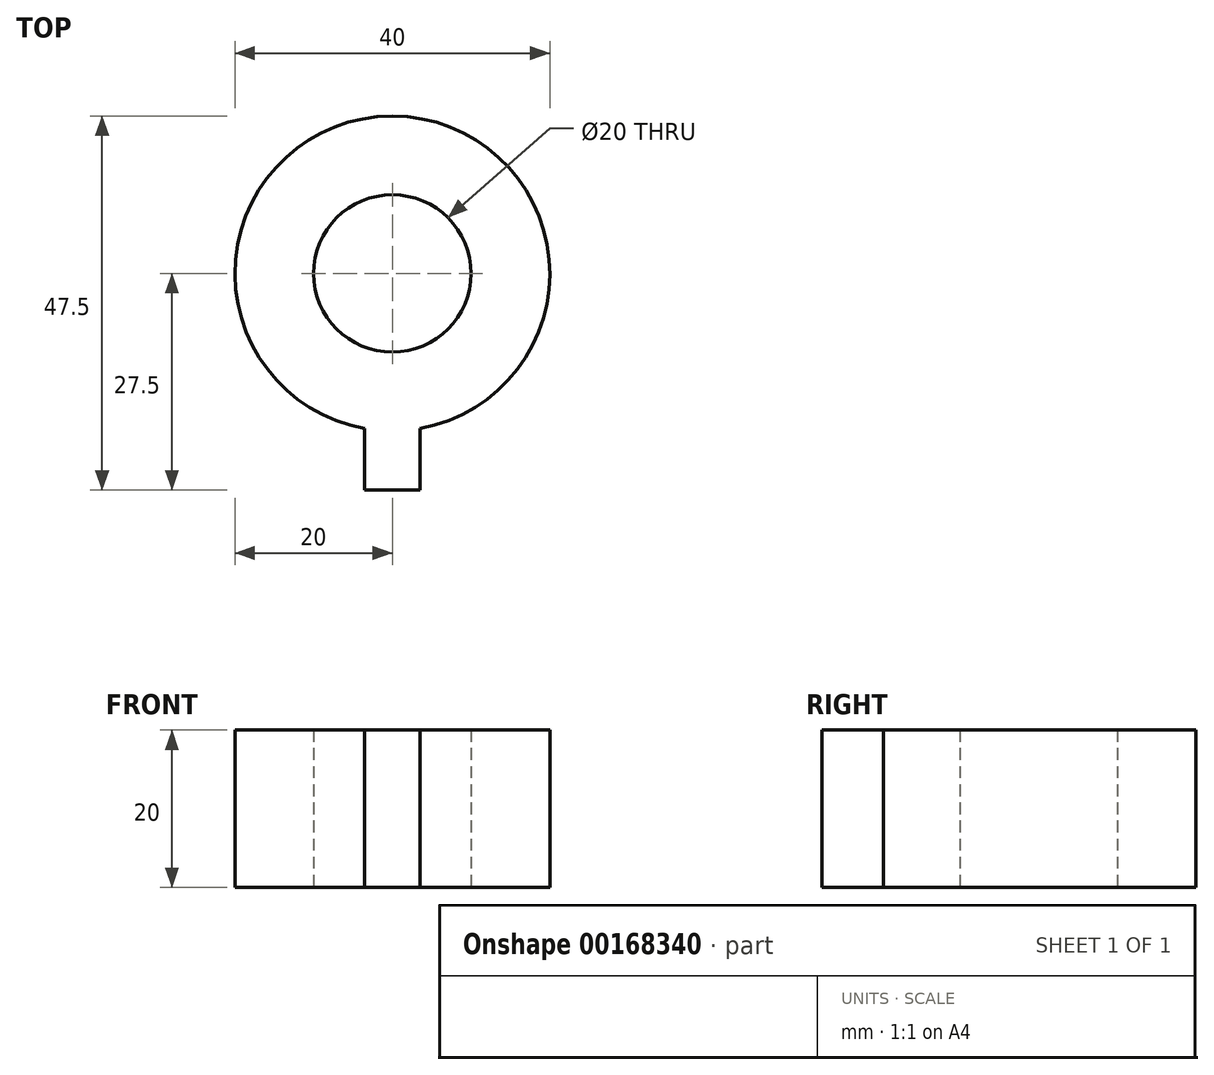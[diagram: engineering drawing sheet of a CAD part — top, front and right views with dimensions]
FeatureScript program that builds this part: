
annotation { "Feature Type Name" : "Feature", "Feature Type Description" : "" }
export const myFeature = defineFeature(function(context is Context, id is Id, definition is map)
    precondition{}
    {
        {
            var Q0;
            Q0=qCreatedBy(makeId("Top.planeOp"),FACE);
            var sketch = newSketch(context, id + "F0", { "sketchPlane" : qUnion([Q0])});
            skCircle(sketch, "E0", {"center": v(0, 0) * mm, "radius": 10 * mm});
            skCircle(sketch, "E1", {"center": v(0, 0) * mm, "radius": 20 * mm});
            skSolve(sketch);
        }
        {
            var Q0;
            Q0 = qSketchRegion(id + "F0", true);
            extrude(context, id + "F1", {"entities" : qUnion([Q0]), "depth" : 20 * mm});
        }
        {
            var Q0;
            Q0=makeQuery(id+"F1.opExtrude","CAP_FACE",FACE,{"disambiguationData":[OSD([sQuery(id+"F0.wireOp",EDGE,"E0"),sQuery(id+"F0.wireOp",EDGE,"E1")])],"isStart":false});
            var sketch = newSketch(context, id + "F2", { "sketchPlane" : qUnion([Q0])});
            skLineSegment(sketch, "E2.bottom", {"start": v(3.5, -27.5) * mm, "end": v(-3.5, -27.5) * mm});
            skLineSegment(sketch, "E2.top", {"start": v(3.5, -12.5) * mm, "end": v(-3.5, -12.5) * mm});
            skLineSegment(sketch, "E2.left", {"start": v(3.5, -27.5) * mm, "end": v(3.5, -12.5) * mm});
            skLineSegment(sketch, "E2.right", {"start": v(-3.5, -27.5) * mm, "end": v(-3.5, -12.5) * mm});
            skPoint(sketch, "E2.middle", {"position": v(0, -20) * mm});
            skSolve(sketch);
        }
        {
            var Q0;
            Q0 = qSketchRegion(id + "F2", true);
            extrude(context, id + "F3", {"entities" : qUnion([Q0]), "operationType" : NewBodyOperationType.ADD, "oppositeDirection" : true, "depth" : 20 * mm});
        }
    });
